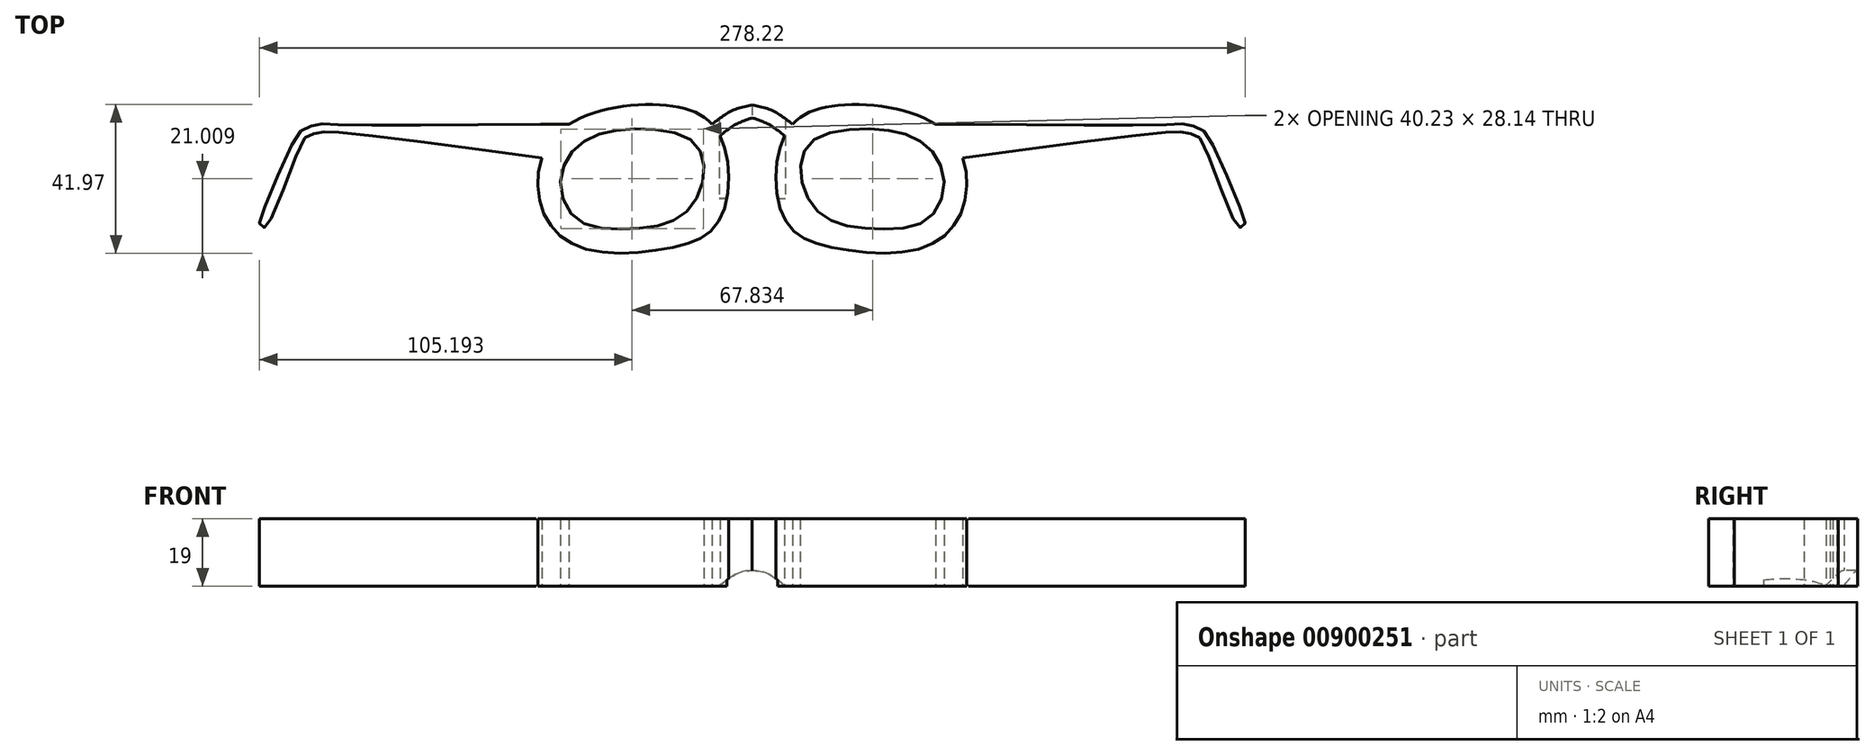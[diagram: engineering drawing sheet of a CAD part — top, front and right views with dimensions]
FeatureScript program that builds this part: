
annotation { "Feature Type Name" : "Feature", "Feature Type Description" : "" }
export const myFeature = defineFeature(function(context is Context, id is Id, definition is map)
    precondition{}
    {
        {
            var Q0;
            Q0=qCreatedBy(makeId("Top.planeOp"),FACE);
            var sketch = newSketch(context, id + "F0", { "sketchPlane" : qUnion([Q0])});
            skLineSegment(sketch, "E0", {"start": v(0, 0) * mm, "end": v(0, 52.97) * mm, "construction": true});
            skPoint(sketch, "E1.2.internal.snap0", {"position": v(0, 26.48) * mm});
            skFitSpline(sketch, "E1", {"points": [v(-7, 10.72) * mm, v(-12.7, 22.26) * mm, v(-26.36, 26.48) * mm, v(-48.95, 22.52) * mm, v(-59.43, 11.43) * mm, v(-58.8, -4.33) * mm, v(-47.05, -14.23) * mm, v(-22.62, -13.8) * mm, v(-9.79, -6.97) * mm, v(-7, 10.72) * mm]});
            skFitSpline(sketch, "E2", {"points": [v(-33.13, 19.65) * mm, v(-47.4, 16.26) * mm, v(-53.99, 6.25) * mm, v(-49.58, -5.8) * mm, v(-34.19, -8.48) * mm, v(-20.35, -5.1) * mm, v(-13.8, 5.77) * mm, v(-16.83, 16.13) * mm, v(-33.13, 19.65) * mm]});
            skLineSegment(sketch, "E3", {"start": v(-51.72, 20.97) * mm, "end": v(-59.81, 20.97) * mm});
            skFitSpline(sketch, "E4", {"points": [v(-59.81, 20.97) * mm, v(-119.25, 20.97) * mm, v(-122.6, 20.97) * mm, v(-126.42, 19.62) * mm, v(-128.98, 17.1) * mm, v(-138.73, -5.39) * mm, v(-138.94, -7.48) * mm, v(-137.88, -8.16) * mm, v(-136.3, -6.74) * mm, v(-127.15, 15.72) * mm, v(-124.88, 18.07) * mm, v(-121.8, 18.68) * mm, v(-119, 18.83) * mm, v(-59.43, 11.43) * mm], "startDerivative": vector(-410.53, -2.42) * mm, "endDerivative": vector(413.2, -56.91) * mm});
            skFitSpline(sketch, "E5", {"points": [v(-11.36, 20.97) * mm, v(-5.9, 24.7) * mm, v(0, 26.48) * mm], "startDerivative": vector(10.4, 8.28) * mm, "endDerivative": vector(12.33, 2.71) * mm});
            skLineSegment(sketch, "E6", {"start": v(0, 26.48) * mm, "end": v(0, 22.8) * mm});
            skFitSpline(sketch, "E7", {"points": [v(0, 22.8) * mm, v(-1.88, 22.1) * mm, v(-4.84, 20.84) * mm, v(-9.1, 17.7) * mm], "startDerivative": vector(-6.98, -2.6) * mm, "endDerivative": vector(-10.43, -8.5) * mm});
            skSolve(sketch);
        }
        {
            var Q0;
            Q0 = qSketchRegion(id + "F0", true);
            extrude(context, id + "F1", {"entities" : qUnion([Q0]), "depth" : 19 * mm, "offsetDistance" : 25 * mm});
        }
        {
            var Q0;
            Q0=makeQuery(id+"F1.opExtrude","SWEPT_BODY",BODY,{"disambiguationData":[OSD([sQuery(id+"F0.wireOp",EDGE,"E1"),sQuery(id+"F0.wireOp",EDGE,"E2"),sQuery(id+"F0.wireOp",EDGE,"E3"),sQuery(id+"F0.wireOp",EDGE,"E4"),sQuery(id+"F0.wireOp",EDGE,"E5"),sQuery(id+"F0.wireOp",EDGE,"E6"),sQuery(id+"F0.wireOp",EDGE,"E7"),sQuery(id+"F0.wireOp",EDGE,"E1")])]});
            var Q1;
            Q1=qCreatedBy(makeId("Right.planeOp"),FACE);
            mirror(context, id + "F2", {"operationType" : NewBodyOperationType.ADD, "entities" : qUnion([Q0]), "mirrorPlane" : qUnion([Q1])});
        }
        {
            var Q0;
            Q0=qCreatedBy(makeId("Front.planeOp"),FACE);
            var sketch = newSketch(context, id + "F3", { "sketchPlane" : qUnion([Q0])});
            skLineSegment(sketch, "E8", {"start": v(0, 0) * mm, "end": v(0, 29.02) * mm});
            skFitSpline(sketch, "E9", {"points": [v(0, 4.42) * mm, v(4.92, 3.26) * mm, v(9.35, 0) * mm, v(10.44, 0) * mm, v(154.69, 0) * mm, v(155.03, 0) * mm], "startDerivative": vector(38.47, -2.8) * mm, "endDerivative": vector(1.68, 0.07) * mm});
            skLineSegment(sketch, "E10", {"start": v(0, 0) * mm, "end": v(9.35, 0) * mm});
            skFitSpline(sketch, "E11.MirrorCS", {"points": [v(0, 4.42) * mm, v(-4.92, 3.26) * mm, v(-9.35, 0) * mm, v(-10.44, 0) * mm, v(-154.69, 0) * mm, v(-155.03, 0) * mm], "startDerivative": vector(-38.47, -2.8) * mm, "endDerivative": vector(-1.68, 0.07) * mm});
            skLineSegment(sketch, "E12.MirrorCS", {"start": v(0, 0) * mm, "end": v(-9.35, 0) * mm});
            skSolve(sketch);
        }
        {
            var Q0;
            Q0 = qSketchRegion(id + "F3", true);
            extrude(context, id + "F4", {"entities" : qUnion([Q0]), "operationType" : NewBodyOperationType.REMOVE, "oppositeDirection" : true, "depth" : 83.3 * mm, "offsetDistance" : 25 * mm});
        }
    });
